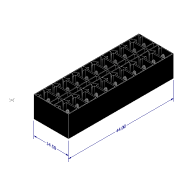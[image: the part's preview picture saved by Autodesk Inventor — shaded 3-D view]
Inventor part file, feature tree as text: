
AUTODESK INVENTOR PART (.ipt)
format: ipt  version: 2022 (Build 260153000, 153)  size: 718,336 bytes
history: native  units: mm
features: sketch x7, projected_geometry x7, extrude x5, other x4, pattern_linear x2, plane x1, loft x1
ambient origin geometry x8: Origin, YZ Plane, XZ Plane, XY Plane, X Axis, Y Axis, Z Axis, Center Point
bodies: Solid1 (feature_tree), Solid2 (feature_tree)
feature tree (27):
  other  "Annotations"
  extrude  "Extrusion1"  Depth=3.5mm
  extrude  "Extrusion2"  Depth=0.2mm
  extrude  "Extrusion3"  Depth=0.25mm
  plane  "Work Plane1"
  loft  "Loft1"
  sketch  "Sketch6"  dims[d8=4.0mm]
  pattern_linear  "Rectangular Pattern1"  Spacing1=2.2mm  [1 undecoded]
  pattern_linear  "Rectangular Pattern2"  Spacing1=7.0mm  [1 undecoded]
  extrude  "Extrusion4"  Depth=0.5mm
  extrude  "Extrusion5"  Depth=14.5mm
  sketch  "Sketch1"  dims[d0=6.0mm d1=3.5mm]
  sketch  "Sketch2"  dims[d2=1.0mm d3=0.2mm]
  sketch  "Sketch3"  dims[d4=0.3mm d5=0.25mm]
  sketch  "Sketch5"  dims[d6=0.25mm d7=6.5mm]
  other  "Edges1"
  sketch  "Sketch7"  dims[d9=8.0mm d10=0.0mm]
  sketch  "Sketch8"  dims[d11=1.0mm d12=0.0mm d13=2.2mm d14=7.0mm d15=0.0mm d16=0.5mm d17=0.3535mm d18=0.0mm d19=90.0deg d20=0.0mm d21=90.0deg d22=110.0mm d24=4.0mm d25=20.0mm d27=8.0mm d28=110.0mm d30=4.0mm d31=20.0mm d33=8.0mm d34=7.0mm d35=0.0mm d36=10.0mm d37=0.0mm d38=5.363844mm d39=3.767974mm d40=44.0mm d41=5.587908mm d42=7.829387mm d43=14.5mm]
  projected_geometry  "Projected Loop1"
  projected_geometry  "Projected Loop2"
  projected_geometry  "Projected Loop3"
  projected_geometry  "Projected Loop4"
  projected_geometry  "Projected Loop5"
  projected_geometry  "Projected Loop6"
  projected_geometry  "Projected Loop7"
  other  "Linear Dimension 1"
  other  "Linear Dimension 2"
note: 2 required parameter values undecoded (feature->parameter linkage not recoverable at this tier; creation-order binding heuristic only, values carry confidence <= 0.55)
